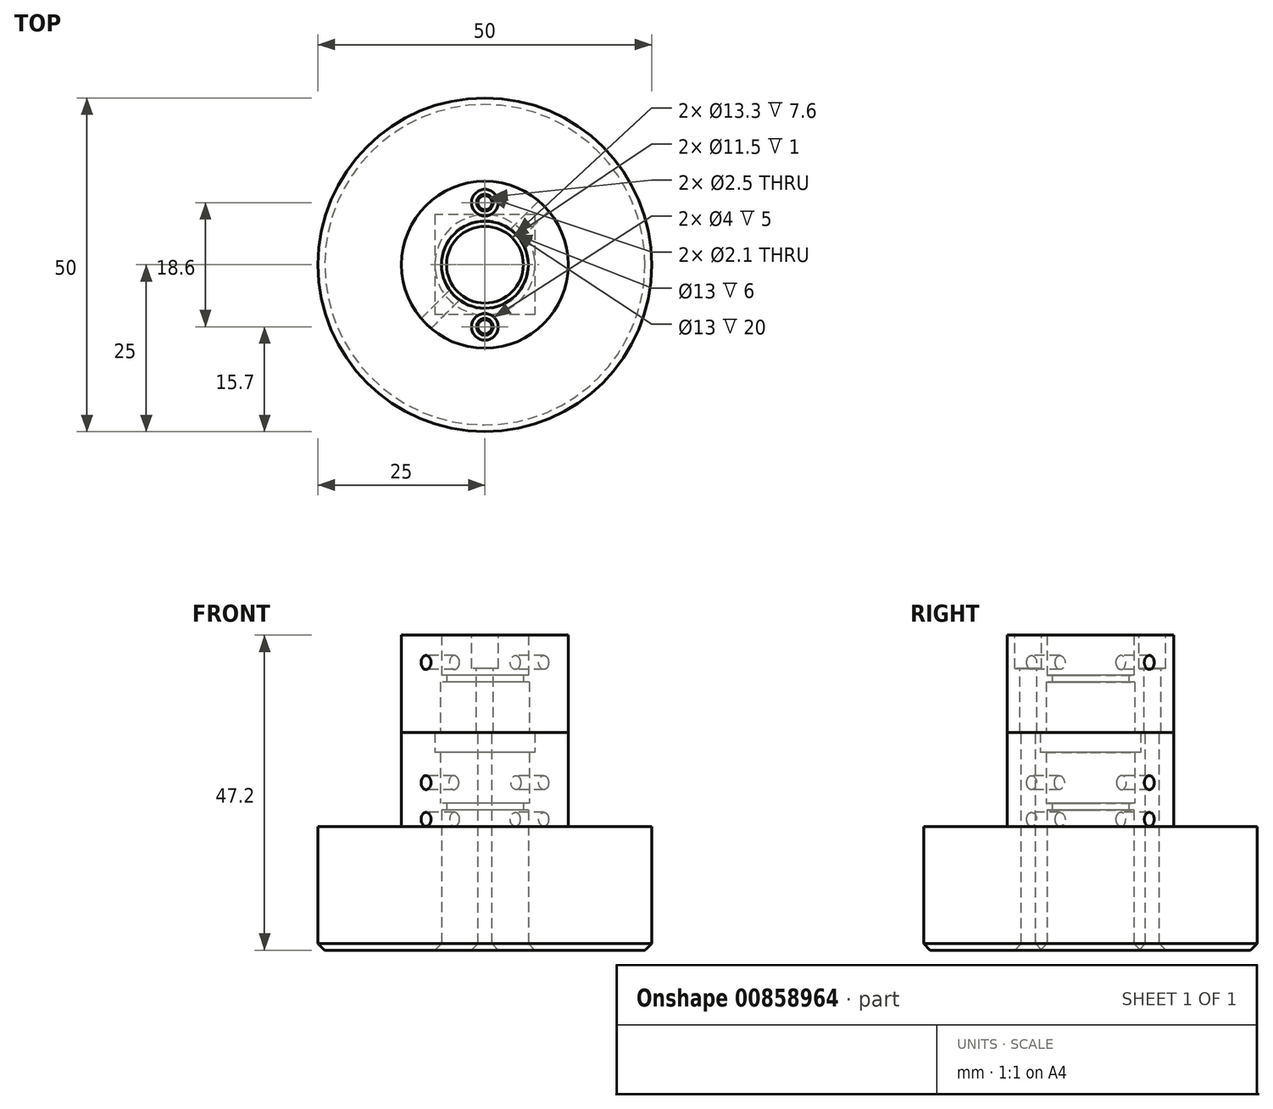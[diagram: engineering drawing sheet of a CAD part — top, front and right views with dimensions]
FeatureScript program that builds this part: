
annotation { "Feature Type Name" : "Feature", "Feature Type Description" : "" }
export const myFeature = defineFeature(function(context is Context, id is Id, definition is map)
    precondition{}
    {
        {
            var Q0;
            Q0=qCreatedBy(makeId("Top.planeOp"),FACE);
            var sketch = newSketch(context, id + "F0", { "sketchPlane" : qUnion([Q0])});
            skCircle(sketch, "E0", {"center": v(0, 0) * mm, "radius": 25 * mm});
            skCircle(sketch, "E1", {"center": v(0, 0) * mm, "radius": 6.5 * mm});
            skSolve(sketch);
        }
        {
            var Q0;
            Q0=qSketchRegion(id+"F0",true);
            extrude(context, id + "F1", {"entities" : qUnion([Q0]), "depth" : 3.5 * mm});
        }
        {
            var Q0;
            Q0=makeQuery(id+"F1.opExtrude","CAP_FACE",FACE,{"disambiguationData":[OSD([sQuery(id+"F0.wireOp",EDGE,"E0"),sQuery(id+"F0.wireOp",EDGE,"E1")])],"isStart":false});
            var sketch = newSketch(context, id + "F2", { "sketchPlane" : qUnion([Q0])});
            skCircle(sketch, "E2", {"center": v(0, 0) * mm, "radius": 6.5 * mm});
            skCircle(sketch, "E3", {"center": v(0, 0) * mm, "radius": 12.5 * mm});
            skSolve(sketch);
        }
        {
            var Q0;
            Q0=qSketchRegion(id+"F2",true);
            extrude(context, id + "F3", {"entities" : qUnion([Q0]), "operationType" : NewBodyOperationType.ADD, "depth" : 2.5 * mm});
        }
        {
            var Q0;
            Q0=makeQuery(id+"F3.opExtrude","CAP_FACE",FACE,{"disambiguationData":[OSD([sQuery(id+"F2.wireOp",EDGE,"E2"),sQuery(id+"F2.wireOp",EDGE,"E3")])],"isStart":false});
            var sketch = newSketch(context, id + "F4", { "sketchPlane" : qUnion([Q0])});
            skCircle(sketch, "E4", {"center": v(0, 0) * mm, "radius": 5.75 * mm});
            skCircle(sketch, "E5", {"center": v(0, 0) * mm, "radius": 12.5 * mm});
            skSolve(sketch);
        }
        {
            var Q0;
            Q0=qSketchRegion(id+"F4",true);
            extrude(context, id + "F5", {"entities" : qUnion([Q0]), "operationType" : NewBodyOperationType.ADD, "depth" : 1 * mm});
        }
        {
            var Q0;
            Q0=makeQuery(id+"F5.opExtrude","CAP_FACE",FACE,{"disambiguationData":[OSD([sQuery(id+"F4.wireOp",EDGE,"E4"),sQuery(id+"F4.wireOp",EDGE,"E5")])],"isStart":false});
            var sketch = newSketch(context, id + "F6", { "sketchPlane" : qUnion([Q0])});
            skCircle(sketch, "E6", {"center": v(0, 0) * mm, "radius": 6.65 * mm});
            skCircle(sketch, "E7", {"center": v(0, 0) * mm, "radius": 12.5 * mm});
            skSolve(sketch);
        }
        {
            var Q0;
            Q0=qSketchRegion(id+"F6",true);
            extrude(context, id + "F7", {"entities" : qUnion([Q0]), "operationType" : NewBodyOperationType.ADD, "depth" : 7.6 * mm});
        }
        {
            var Q0;
            Q0=makeQuery(id+"F7.opExtrude","CAP_FACE",FACE,{"disambiguationData":[OSD([sQuery(id+"F6.wireOp",EDGE,"E6"),sQuery(id+"F6.wireOp",EDGE,"E7")])],"isStart":false});
            var sketch = newSketch(context, id + "F8", { "sketchPlane" : qUnion([Q0])});
            skLineSegment(sketch, "E8.rect.bottom", {"start": v(7.5, 7.5) * mm, "end": v(-7.5, 7.5) * mm});
            skLineSegment(sketch, "E8.rect.top", {"start": v(7.5, -7.5) * mm, "end": v(-7.5, -7.5) * mm});
            skLineSegment(sketch, "E8.rect.left", {"start": v(7.5, 7.5) * mm, "end": v(7.5, -7.5) * mm});
            skLineSegment(sketch, "E8.rect.right", {"start": v(-7.5, 7.5) * mm, "end": v(-7.5, -7.5) * mm});
            skPoint(sketch, "E8.rect.middle", {"position": v(0, 0) * mm});
            skCircle(sketch, "E9", {"center": v(0, 0) * mm, "radius": 12.5 * mm});
            skSolve(sketch);
        }
        {
            var Q0;
            Q0=qSketchRegion(id+"F8",true);
            extrude(context, id + "F9", {"entities" : qUnion([Q0]), "operationType" : NewBodyOperationType.ADD, "depth" : 3 * mm});
        }
        {
            var Q0;
            Q0=makeQuery(id+"F9.opExtrude","CAP_FACE",FACE,{"disambiguationData":[OSD([sQuery(id+"F8.wireOp",EDGE,"E8.rect.bottom"),sQuery(id+"F8.wireOp",EDGE,"E8.rect.top"),sQuery(id+"F8.wireOp",EDGE,"E8.rect.left"),sQuery(id+"F8.wireOp",EDGE,"E8.rect.right"),sQuery(id+"F8.wireOp",EDGE,"E9")])],"isStart":false});
            var sketch = newSketch(context, id + "F10", { "sketchPlane" : qUnion([Q0])});
            skCircle(sketch, "E10", {"center": v(0, 0) * mm, "radius": 6.65 * mm});
            skCircle(sketch, "E11", {"center": v(0, 0) * mm, "radius": 12.5 * mm});
            skSolve(sketch);
        }
        {
            var Q0;
            Q0=qSketchRegion(id+"F10",true);
            extrude(context, id + "F11", {"entities" : qUnion([Q0]), "depth" : 7.6 * mm});
        }
        {
            var Q0;
            Q0=makeQuery(id+"F11.opExtrude","CAP_FACE",FACE,{"disambiguationData":[OSD([sQuery(id+"F10.wireOp",EDGE,"E10"),sQuery(id+"F10.wireOp",EDGE,"E11")])],"isStart":false});
            var sketch = newSketch(context, id + "F12", { "sketchPlane" : qUnion([Q0])});
            skCircle(sketch, "E12", {"center": v(0, 0) * mm, "radius": 5.75 * mm});
            skCircle(sketch, "E13", {"center": v(0, 0) * mm, "radius": 12.5 * mm});
            skSolve(sketch);
        }
        {
            var Q0;
            Q0=qSketchRegion(id+"F12",true);
            extrude(context, id + "F13", {"entities" : qUnion([Q0]), "operationType" : NewBodyOperationType.ADD, "depth" : 1 * mm});
        }
        {
            var Q0;
            Q0=makeQuery(id+"F13.opExtrude","CAP_FACE",FACE,{"disambiguationData":[OSD([sQuery(id+"F12.wireOp",EDGE,"E12"),sQuery(id+"F12.wireOp",EDGE,"E13")])],"isStart":false});
            var sketch = newSketch(context, id + "F14", { "sketchPlane" : qUnion([Q0])});
            skCircle(sketch, "E14", {"center": v(0, 0) * mm, "radius": 6.5 * mm});
            skCircle(sketch, "E15", {"center": v(0, 0) * mm, "radius": 12.5 * mm});
            skSolve(sketch);
        }
        {
            var Q0;
            Q0=qSketchRegion(id+"F14",true);
            extrude(context, id + "F15", {"entities" : qUnion([Q0]), "operationType" : NewBodyOperationType.ADD, "depth" : 6 * mm});
        }
        {
            var Q0;
            Q0=makeQuery(id+"F15.opExtrude","CAP_FACE",FACE,{"disambiguationData":[OSD([sQuery(id+"F14.wireOp",EDGE,"E14"),sQuery(id+"F14.wireOp",EDGE,"E15")])],"isStart":false});
            var sketch = newSketch(context, id + "F16", { "sketchPlane" : qUnion([Q0])});
            skLineSegment(sketch, "E16", {"start": v(0, 0) * mm, "end": v(-9.3, 0) * mm});
            skLineSegment(sketch, "E17", {"start": v(0, 0) * mm, "end": v(0, 9.3) * mm});
            skLineSegment(sketch, "E18", {"start": v(0, 0) * mm, "end": v(9.3, 0) * mm});
            skLineSegment(sketch, "E19", {"start": v(0, 0) * mm, "end": v(0, -9.3) * mm});
            skLineSegment(sketch, "E20", {"start": v(0, 0) * mm, "end": v(-6.63, 6.63) * mm});
            skSolve(sketch);
        }
        {
            var Q0;
            Q0=sQuery(id+"F16.wireOp",VERTEX,"E17.end");
            var Q1;
            Q1=sQuery(id+"F16.wireOp",VERTEX,"E19.end");
            var Q2;
            Q2=makeQuery(id+"F11.opExtrude","SWEPT_BODY",BODY,{"disambiguationData":[OSD([sQuery(id+"F10.wireOp",EDGE,"E10"),sQuery(id+"F10.wireOp",EDGE,"E11")])]});
            hole(context, id + "F17", {"style" : HoleStyle.C_BORE, "holeDiameter" : 2.5 * mm, "cBoreDiameter" : 4 * mm, "cBoreDepth" : 5 * mm, "endStyle" : HoleEndStyle.THROUGH, "locations" : qUnion([Q0, Q1]), "scope" : qUnion([Q2]), "isTappedThrough" : true});
        }
        {
            var Q0;
            Q0=sQuery(id+"F16.wireOp",VERTEX,"E17.end");
            var Q1;
            Q1=sQuery(id+"F16.wireOp",VERTEX,"E19.end");
            var Q2;
            Q2=makeQuery(id+"F1.opExtrude","SWEPT_BODY",BODY,{"disambiguationData":[OSD([sQuery(id+"F0.wireOp",EDGE,"E0"),sQuery(id+"F0.wireOp",EDGE,"E1")])]});
            hole(context, id + "F18", {"style" : HoleStyle.SIMPLE, "holeDiameter" : 2.1 * mm, "endStyle" : HoleEndStyle.THROUGH, "locations" : qUnion([Q0, Q1]), "scope" : qUnion([Q2]), "isTappedThrough" : true});
        }
        {
            var Q0;
            Q0=makeQuery(id+"F16.imprint","IMPRINT",FACE,{"disambiguationData":[TD([[makeQuery(id+"F16.imprint","IMPRINT",EDGE,{"derivedFrom":makeQuery(id+"F15.opExtrude","CAP_EDGE",EDGE,{"disambiguationData":[OSD([sQuery(id+"F14.wireOp",EDGE,"E15")])],"isStart":false})}),1.0]])]});
            var Q1;
            Q1=sQuery(id+"F16.wireOp",EDGE,"E20");
            cPlane(context, id + "F19", {"entities" : qUnion([Q0, Q1]), "cplaneType" : CPlaneType.LINE_ANGLE, "offset" : 150 * mm, "angle" : 90 * degree, "width" : 150 * mm, "height" : 150 * mm});
        }
        {
            var Q0;
            Q0=qCreatedBy(id+"F19.planeOp",FACE);
            cPlane(context, id + "F20", {"entities" : qUnion([Q0]), "cplaneType" : CPlaneType.OFFSET, "offset" : 50 * mm, "width" : 150 * mm, "height" : 150 * mm});
        }
        {
            var Q0;
            Q0=qCreatedBy(id+"F20.planeOp",FACE);
            var sketch = newSketch(context, id + "F21", { "sketchPlane" : qUnion([Q0])});
            skPoint(sketch, "E21", {"position": v(0, 4.6) * mm});
            skPoint(sketch, "E22", {"position": v(0, 10.1) * mm});
            skPoint(sketch, "E23", {"position": v(0, 28.1) * mm});
            skSolve(sketch);
        }
        {
            var Q0;
            Q0=sQuery(id+"F21.wireOp",VERTEX,"E23");
            var Q1;
            Q1=sQuery(id+"F21.wireOp",VERTEX,"E22");
            var Q2;
            Q2=sQuery(id+"F21.wireOp",VERTEX,"E21");
            var Q3;
            Q3=makeQuery(id+"F11.opExtrude","SWEPT_BODY",BODY,{"disambiguationData":[OSD([sQuery(id+"F10.wireOp",EDGE,"E10"),sQuery(id+"F10.wireOp",EDGE,"E11")])]});
            var Q4;
            Q4=makeQuery(id+"F1.opExtrude","SWEPT_BODY",BODY,{"disambiguationData":[OSD([sQuery(id+"F0.wireOp",EDGE,"E0"),sQuery(id+"F0.wireOp",EDGE,"E1")])]});
            hole(context, id + "F22", {"style" : HoleStyle.SIMPLE, "holeDiameter" : 2.1 * mm, "endStyle" : HoleEndStyle.THROUGH, "locations" : qUnion([Q0, Q1, Q2]), "scope" : qUnion([Q3, Q4])});
        }
        {
            var Q0;
            Q0=makeQuery(id+"F1.opExtrude","CAP_FACE",FACE,{"disambiguationData":[OSD([sQuery(id+"F0.wireOp",EDGE,"E0"),sQuery(id+"F0.wireOp",EDGE,"E1")])],"isStart":true});
            extrude(context, id + "F23", {"entities" : qUnion([Q0]), "operationType" : NewBodyOperationType.ADD, "depth" : 15 * mm, "offsetDistance" : 25 * mm});
        }
        {
            var Q0;
            Q0=makeQuery(id+"F23.opExtrude","CAP_FACE",FACE,{"disambiguationData":[OSD([sQuery(id+"F0.wireOp",EDGE,"E0"),sQuery(id+"F0.wireOp",EDGE,"E1")])],"isStart":false});
            chamfer(context, id + "F24", {"entities" : qUnion([Q0]), "width" : 1 * mm, "tangentPropagation" : true});
        }
    });
